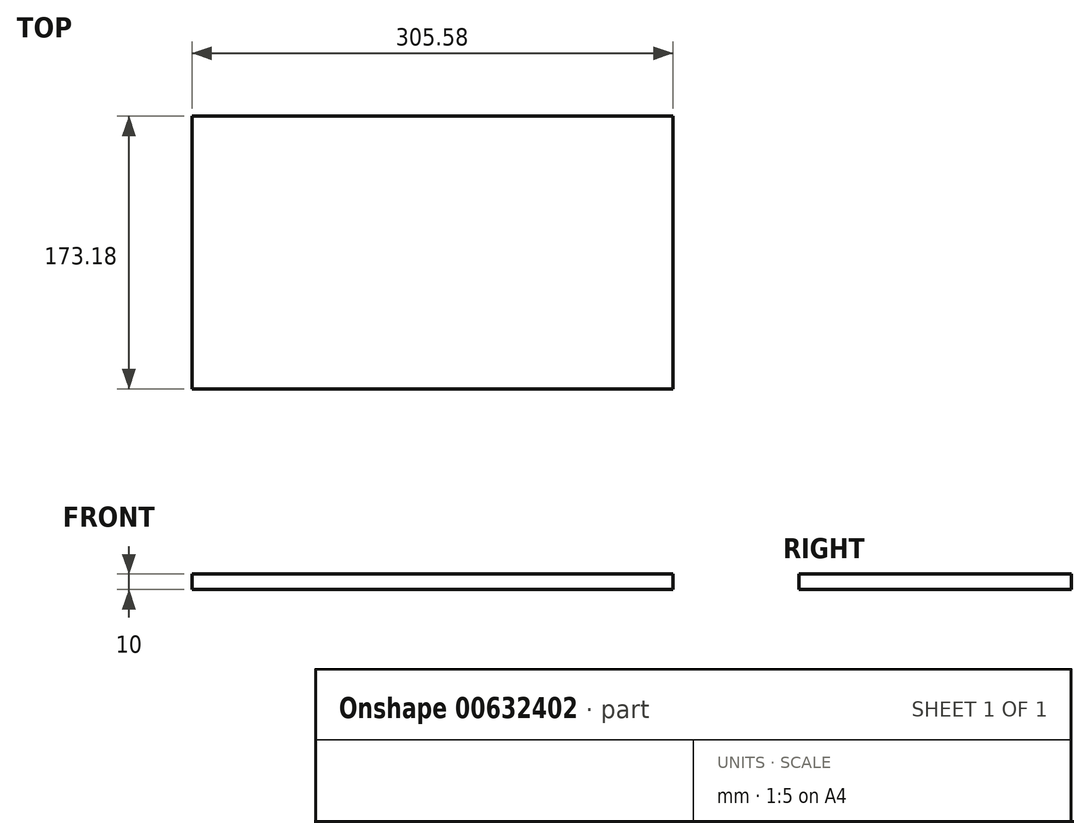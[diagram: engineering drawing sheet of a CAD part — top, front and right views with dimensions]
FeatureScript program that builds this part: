
annotation { "Feature Type Name" : "Feature", "Feature Type Description" : "" }
export const myFeature = defineFeature(function(context is Context, id is Id, definition is map)
    precondition{}
    {
        {
            var Q0;
            Q0=qCreatedBy(makeId("Top.planeOp"),FACE);
            var sketch = newSketch(context, id + "F0", { "sketchPlane" : qUnion([Q0])});
            skLineSegment(sketch, "E0.bottom", {"start": v(152.8, 86.6) * mm, "end": v(-152.8, 86.6) * mm});
            skLineSegment(sketch, "E0.top", {"start": v(152.8, -86.6) * mm, "end": v(-152.8, -86.6) * mm});
            skLineSegment(sketch, "E0.left", {"start": v(152.8, 86.6) * mm, "end": v(152.8, -86.6) * mm});
            skLineSegment(sketch, "E0.right", {"start": v(-152.8, 86.6) * mm, "end": v(-152.8, -86.6) * mm});
            skPoint(sketch, "E0.middle", {"position": v(0, 0) * mm});
            skSolve(sketch);
        }
        {
            var Q0;
            Q0 = qSketchRegion(id + "F0", true);
            extrude(context, id + "F1", {"entities" : qUnion([Q0]), "depth" : 10 * mm, "offsetDistance" : 25.4 * mm});
        }
    });
